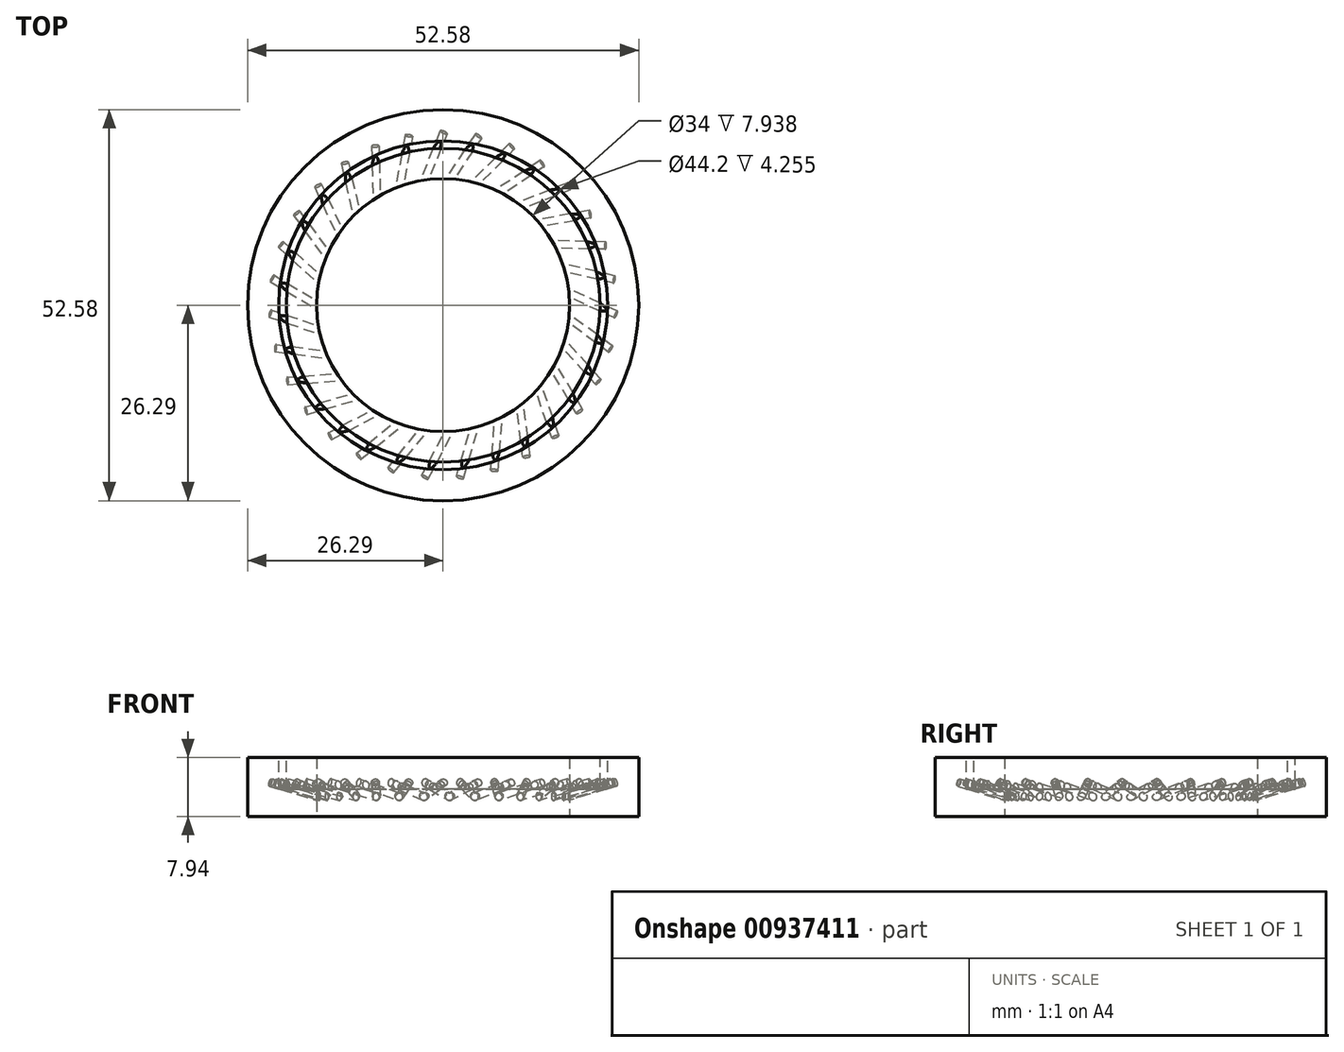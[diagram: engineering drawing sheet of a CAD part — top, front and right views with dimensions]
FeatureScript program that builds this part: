
annotation { "Feature Type Name" : "Feature", "Feature Type Description" : "" }
export const myFeature = defineFeature(function(context is Context, id is Id, definition is map)
    precondition{}
    {
        {
            var Q0;
            Q0=qCreatedBy(makeId("Top.planeOp"),FACE);
            var sketch = newSketch(context, id + "F0", { "sketchPlane" : qUnion([Q0])});
            skCircle(sketch, "E0", {"center": v(0, 0) * mm, "radius": 26.29 * mm});
            skSolve(sketch);
        }
        {
            var Q0;
            Q0=makeQuery(id+"F0.imprint","IMPRINT",FACE,{"disambiguationData":[TD([[makeQuery(id+"F0.imprint","IMPRINT",EDGE,{"derivedFrom":sQuery(id+"F0.wireOp",EDGE,"E0")}),1.0]])]});
            extrude(context, id + "F1", {"entities" : qUnion([Q0]), "depth" : 7.94 * mm, "offsetDistance" : 25.4 * mm});
        }
        {
            var Q0;
            Q0=qCreatedBy(makeId("Top.planeOp"),FACE);
            var sketch = newSketch(context, id + "F2", { "sketchPlane" : qUnion([Q0])});
            skCircle(sketch, "E1", {"center": v(0, 0) * mm, "radius": 17 * mm});
            skSolve(sketch);
        }
        {
            var Q0;
            Q0=qSketchRegion(id+"F2",true);
            extrude(context, id + "F3", {"entities" : qUnion([Q0]), "operationType" : NewBodyOperationType.REMOVE, "endBound" : BoundingType.THROUGH_ALL, "depth" : 7.94 * mm, "offsetDistance" : 25.4 * mm});
        }
        {
            var Q0;
            Q0=qCreatedBy(makeId("Right.planeOp"),FACE);
            var sketch = newSketch(context, id + "F4", { "sketchPlane" : qUnion([Q0])});
            skLineSegment(sketch, "E2", {"start": v(0, 0) * mm, "end": v(0, 143.33) * mm});
            skLineSegment(sketch, "E3", {"start": v(-8.9, 0) * mm, "end": v(-8.9, 70.97) * mm});
            skSolve(sketch);
        }
        {
            var Q0;
            Q0=qCreatedBy(makeId("Top.planeOp"),FACE);
            var sketch = newSketch(context, id + "F5", { "sketchPlane" : qUnion([Q0])});
            skLineSegment(sketch, "E4", {"start": v(0, 0) * mm, "end": v(29.86, 0) * mm});
            skSolve(sketch);
        }
        {
            var Q0;
            Q0=qCreatedBy(makeId("Right.planeOp"),FACE);
            var sketch = newSketch(context, id + "F6", { "sketchPlane" : qUnion([Q0])});
            skCircle(sketch, "E5", {"center": v(0, 54.1) * mm, "radius": 0.5 * mm});
            skSolve(sketch);
        }
        {
            var Q0;
            Q0=makeQuery(id+"F6.imprint","IMPRINT",FACE,{"disambiguationData":[TD([[makeQuery(id+"F6.imprint","IMPRINT",EDGE,{"derivedFrom":sQuery(id+"F6.wireOp",EDGE,"E5")}),1.0]])]});
            extrude(context, id + "F7", {"entities" : qUnion([Q0]), "depth" : 28.07 * mm, "offsetDistance" : 25.4 * mm});
        }
        {
            var Q0;
            Q0=makeQuery(id+"F7.opExtrude","SWEPT_BODY",BODY,{"disambiguationData":[OSD([sQuery(id+"F6.wireOp",EDGE,"E5")])]});
            var Q1;
            Q1=sQuery(id+"F4.wireOp",EDGE,"E2");
            transform(context, id + "F8", {"entities" : qUnion([Q0]), "transformType" : TransformType.ROTATION, "transformAxis" : qUnion([Q1]), "angle" : 20 * degree, "makeCopy" : false});
        }
        {
            var Q0;
            Q0=makeQuery(id+"F7.opExtrude","SWEPT_BODY",BODY,{"disambiguationData":[OSD([sQuery(id+"F6.wireOp",EDGE,"E5")])]});
            transform(context, id + "F9", {"entities" : qUnion([Q0]), "transformType" : TransformType.TRANSLATION_3D, "dx" : 0 * mm, "dy" : 0 * mm, "dz" : -58.42 * mm, "makeCopy" : false});
        }
        {
            var Q0;
            Q0=makeQuery(id+"F7.opExtrude","SWEPT_BODY",BODY,{"disambiguationData":[OSD([sQuery(id+"F6.wireOp",EDGE,"E5")])]});
            var Q1;
            Q1=sQuery(id+"F5.wireOp",EDGE,"E4");
            var Q2;
            Q2=sQuery(id+"F5.wireOp",EDGE,"E4");
            transform(context, id + "F10", {"entities" : qUnion([Q0]), "transformType" : TransformType.ROTATION, "transformAxis" : qUnion([Q2]), "angle" : 50 * degree, "makeCopy" : false});
        }
        {
            var Q0;
            Q0=makeQuery(id+"F7.opExtrude","SWEPT_BODY",BODY,{"disambiguationData":[OSD([sQuery(id+"F6.wireOp",EDGE,"E5")])]});
            var Q1;
            Q1=sQuery(id+"F4.wireOp",EDGE,"E2");
            var Q2;
            Q2=sQuery(id+"F4.wireOp",EDGE,"E3");
            transform(context, id + "F11", {"entities" : qUnion([Q0]), "transformType" : TransformType.ROTATION, "transformAxis" : qUnion([Q2]), "angle" : 55 * degree, "makeCopy" : false});
        }
        {
            var Q0;
            Q0=makeQuery(id+"F7.opExtrude","SWEPT_BODY",BODY,{"disambiguationData":[OSD([sQuery(id+"F6.wireOp",EDGE,"E5")])]});
            var Q1;
            Q1=sQuery(id+"F4.wireOp",EDGE,"E2");
            circularPattern(context, id + "F12", {"entities" : qUnion([Q0]), "axis" : qUnion([Q1]), "angle" : 360 * degree, "instanceCount" : 31, "equalSpace" : true});
        }
        {
            var Q0;
            Q0=makeQuery(id+"F7.opExtrude","SWEPT_BODY",BODY,{"disambiguationData":[OSD([sQuery(id+"F6.wireOp",EDGE,"E5")])]});
            var Q1;
            Q1=makeQuery(id+"F12.opPattern","COPY",BODY,{"derivedFrom":makeQuery(id+"F7.opExtrude","SWEPT_BODY",BODY,{"disambiguationData":[OSD([sQuery(id+"F6.wireOp",EDGE,"E5")])]}),"instanceName":"14"});
            var Q2;
            Q2=makeQuery(id+"F1.opExtrude","SWEPT_BODY",BODY,{"disambiguationData":[OSD([sQuery(id+"F0.wireOp",EDGE,"E0")])]});
            booleanBodies(context, id + "F13", {"operationType" : BooleanOperationType.SUBTRACTION, "tools" : qUnion([Q0, Q1]), "targets" : qUnion([Q2])});
        }
        {
            var Q0;
            Q0=makeQuery(id+"F12.opPattern","COPY",BODY,{"derivedFrom":makeQuery(id+"F7.opExtrude","SWEPT_BODY",BODY,{"disambiguationData":[OSD([sQuery(id+"F6.wireOp",EDGE,"E5")])]}),"instanceName":"30"});
            var Q1;
            Q1=makeQuery(id+"F12.opPattern","COPY",BODY,{"derivedFrom":makeQuery(id+"F7.opExtrude","SWEPT_BODY",BODY,{"disambiguationData":[OSD([sQuery(id+"F6.wireOp",EDGE,"E5")])]}),"instanceName":"28"});
            var Q2;
            Q2=makeQuery(id+"F12.opPattern","COPY",BODY,{"derivedFrom":makeQuery(id+"F7.opExtrude","SWEPT_BODY",BODY,{"disambiguationData":[OSD([sQuery(id+"F6.wireOp",EDGE,"E5")])]}),"instanceName":"26"});
            var Q3;
            Q3=makeQuery(id+"F12.opPattern","COPY",BODY,{"derivedFrom":makeQuery(id+"F7.opExtrude","SWEPT_BODY",BODY,{"disambiguationData":[OSD([sQuery(id+"F6.wireOp",EDGE,"E5")])]}),"instanceName":"24"});
            var Q4;
            Q4=makeQuery(id+"F12.opPattern","COPY",BODY,{"derivedFrom":makeQuery(id+"F7.opExtrude","SWEPT_BODY",BODY,{"disambiguationData":[OSD([sQuery(id+"F6.wireOp",EDGE,"E5")])]}),"instanceName":"22"});
            var Q5;
            Q5=makeQuery(id+"F1.opExtrude","SWEPT_BODY",BODY,{"disambiguationData":[OSD([sQuery(id+"F0.wireOp",EDGE,"E0")])]});
            booleanBodies(context, id + "F14", {"operationType" : BooleanOperationType.SUBTRACTION, "tools" : qUnion([Q0, Q1, Q2, Q3, Q4]), "targets" : qUnion([Q5])});
        }
        {
            var Q0;
            Q0=makeQuery(id+"F12.opPattern","COPY",BODY,{"derivedFrom":makeQuery(id+"F7.opExtrude","SWEPT_BODY",BODY,{"disambiguationData":[OSD([sQuery(id+"F6.wireOp",EDGE,"E5")])]}),"instanceName":"20"});
            var Q1;
            Q1=makeQuery(id+"F12.opPattern","COPY",BODY,{"derivedFrom":makeQuery(id+"F7.opExtrude","SWEPT_BODY",BODY,{"disambiguationData":[OSD([sQuery(id+"F6.wireOp",EDGE,"E5")])]}),"instanceName":"18"});
            var Q2;
            Q2=makeQuery(id+"F12.opPattern","COPY",BODY,{"derivedFrom":makeQuery(id+"F7.opExtrude","SWEPT_BODY",BODY,{"disambiguationData":[OSD([sQuery(id+"F6.wireOp",EDGE,"E5")])]}),"instanceName":"16"});
            var Q3;
            Q3=makeQuery(id+"F12.opPattern","COPY",BODY,{"derivedFrom":makeQuery(id+"F7.opExtrude","SWEPT_BODY",BODY,{"disambiguationData":[OSD([sQuery(id+"F6.wireOp",EDGE,"E5")])]}),"instanceName":"13"});
            var Q4;
            Q4=makeQuery(id+"F12.opPattern","COPY",BODY,{"derivedFrom":makeQuery(id+"F7.opExtrude","SWEPT_BODY",BODY,{"disambiguationData":[OSD([sQuery(id+"F6.wireOp",EDGE,"E5")])]}),"instanceName":"11"});
            var Q5;
            Q5=makeQuery(id+"F12.opPattern","COPY",BODY,{"derivedFrom":makeQuery(id+"F7.opExtrude","SWEPT_BODY",BODY,{"disambiguationData":[OSD([sQuery(id+"F6.wireOp",EDGE,"E5")])]}),"instanceName":"9"});
            var Q6;
            Q6=makeQuery(id+"F12.opPattern","COPY",BODY,{"derivedFrom":makeQuery(id+"F7.opExtrude","SWEPT_BODY",BODY,{"disambiguationData":[OSD([sQuery(id+"F6.wireOp",EDGE,"E5")])]}),"instanceName":"7"});
            var Q7;
            Q7=makeQuery(id+"F12.opPattern","COPY",BODY,{"derivedFrom":makeQuery(id+"F7.opExtrude","SWEPT_BODY",BODY,{"disambiguationData":[OSD([sQuery(id+"F6.wireOp",EDGE,"E5")])]}),"instanceName":"5"});
            var Q8;
            Q8=makeQuery(id+"F12.opPattern","COPY",BODY,{"derivedFrom":makeQuery(id+"F7.opExtrude","SWEPT_BODY",BODY,{"disambiguationData":[OSD([sQuery(id+"F6.wireOp",EDGE,"E5")])]}),"instanceName":"3"});
            var Q9;
            Q9=makeQuery(id+"F12.opPattern","COPY",BODY,{"derivedFrom":makeQuery(id+"F7.opExtrude","SWEPT_BODY",BODY,{"disambiguationData":[OSD([sQuery(id+"F6.wireOp",EDGE,"E5")])]}),"instanceName":"1"});
            var Q10;
            Q10=makeQuery(id+"F1.opExtrude","SWEPT_BODY",BODY,{"disambiguationData":[OSD([sQuery(id+"F0.wireOp",EDGE,"E0")])]});
            booleanBodies(context, id + "F15", {"operationType" : BooleanOperationType.SUBTRACTION, "tools" : qUnion([Q0, Q1, Q2, Q3, Q4, Q5, Q6, Q7, Q8, Q9]), "targets" : qUnion([Q10])});
        }
        {
            var Q0;
            Q0=makeQuery(id+"F12.opPattern","COPY",BODY,{"derivedFrom":makeQuery(id+"F7.opExtrude","SWEPT_BODY",BODY,{"disambiguationData":[OSD([sQuery(id+"F6.wireOp",EDGE,"E5")])]}),"instanceName":"29"});
            var Q1;
            Q1=makeQuery(id+"F12.opPattern","COPY",BODY,{"derivedFrom":makeQuery(id+"F7.opExtrude","SWEPT_BODY",BODY,{"disambiguationData":[OSD([sQuery(id+"F6.wireOp",EDGE,"E5")])]}),"instanceName":"27"});
            var Q2;
            Q2=makeQuery(id+"F12.opPattern","COPY",BODY,{"derivedFrom":makeQuery(id+"F7.opExtrude","SWEPT_BODY",BODY,{"disambiguationData":[OSD([sQuery(id+"F6.wireOp",EDGE,"E5")])]}),"instanceName":"25"});
            var Q3;
            Q3=makeQuery(id+"F12.opPattern","COPY",BODY,{"derivedFrom":makeQuery(id+"F7.opExtrude","SWEPT_BODY",BODY,{"disambiguationData":[OSD([sQuery(id+"F6.wireOp",EDGE,"E5")])]}),"instanceName":"23"});
            var Q4;
            Q4=makeQuery(id+"F12.opPattern","COPY",BODY,{"derivedFrom":makeQuery(id+"F7.opExtrude","SWEPT_BODY",BODY,{"disambiguationData":[OSD([sQuery(id+"F6.wireOp",EDGE,"E5")])]}),"instanceName":"21"});
            var Q5;
            Q5=makeQuery(id+"F12.opPattern","COPY",BODY,{"derivedFrom":makeQuery(id+"F7.opExtrude","SWEPT_BODY",BODY,{"disambiguationData":[OSD([sQuery(id+"F6.wireOp",EDGE,"E5")])]}),"instanceName":"19"});
            var Q6;
            Q6=makeQuery(id+"F12.opPattern","COPY",BODY,{"derivedFrom":makeQuery(id+"F7.opExtrude","SWEPT_BODY",BODY,{"disambiguationData":[OSD([sQuery(id+"F6.wireOp",EDGE,"E5")])]}),"instanceName":"17"});
            var Q7;
            Q7=makeQuery(id+"F12.opPattern","COPY",BODY,{"derivedFrom":makeQuery(id+"F7.opExtrude","SWEPT_BODY",BODY,{"disambiguationData":[OSD([sQuery(id+"F6.wireOp",EDGE,"E5")])]}),"instanceName":"15"});
            var Q8;
            Q8=makeQuery(id+"F12.opPattern","COPY",BODY,{"derivedFrom":makeQuery(id+"F7.opExtrude","SWEPT_BODY",BODY,{"disambiguationData":[OSD([sQuery(id+"F6.wireOp",EDGE,"E5")])]}),"instanceName":"12"});
            var Q9;
            Q9=makeQuery(id+"F12.opPattern","COPY",BODY,{"derivedFrom":makeQuery(id+"F7.opExtrude","SWEPT_BODY",BODY,{"disambiguationData":[OSD([sQuery(id+"F6.wireOp",EDGE,"E5")])]}),"instanceName":"10"});
            var Q10;
            Q10=makeQuery(id+"F12.opPattern","COPY",BODY,{"derivedFrom":makeQuery(id+"F7.opExtrude","SWEPT_BODY",BODY,{"disambiguationData":[OSD([sQuery(id+"F6.wireOp",EDGE,"E5")])]}),"instanceName":"8"});
            var Q11;
            Q11=makeQuery(id+"F12.opPattern","COPY",BODY,{"derivedFrom":makeQuery(id+"F7.opExtrude","SWEPT_BODY",BODY,{"disambiguationData":[OSD([sQuery(id+"F6.wireOp",EDGE,"E5")])]}),"instanceName":"6"});
            var Q12;
            Q12=makeQuery(id+"F12.opPattern","COPY",BODY,{"derivedFrom":makeQuery(id+"F7.opExtrude","SWEPT_BODY",BODY,{"disambiguationData":[OSD([sQuery(id+"F6.wireOp",EDGE,"E5")])]}),"instanceName":"4"});
            var Q13;
            Q13=makeQuery(id+"F12.opPattern","COPY",BODY,{"derivedFrom":makeQuery(id+"F7.opExtrude","SWEPT_BODY",BODY,{"disambiguationData":[OSD([sQuery(id+"F6.wireOp",EDGE,"E5")])]}),"instanceName":"2"});
            var Q14;
            Q14=makeQuery(id+"F1.opExtrude","SWEPT_BODY",BODY,{"disambiguationData":[OSD([sQuery(id+"F0.wireOp",EDGE,"E0")])]});
            booleanBodies(context, id + "F16", {"operationType" : BooleanOperationType.SUBTRACTION, "tools" : qUnion([Q0, Q1, Q2, Q3, Q4, Q5, Q6, Q7, Q8, Q9, Q10, Q11, Q12, Q13]), "targets" : qUnion([Q14])});
        }
        {
            var Q0;
            Q0=makeQuery(id+"F1.opExtrude","CAP_FACE",FACE,{"disambiguationData":[OSD([sQuery(id+"F0.wireOp",EDGE,"E0")])],"isStart":false});
            var sketch = newSketch(context, id + "F17", { "sketchPlane" : qUnion([Q0])});
            skCircle(sketch, "E6", {"center": v(0, 0) * mm, "radius": 22.1 * mm});
            skCircle(sketch, "E7", {"center": v(0, 0) * mm, "radius": 21.08 * mm});
            skSolve(sketch);
        }
        {
            var Q0;
            Q0=makeQuery(id+"F17.imprint","IMPRINT",FACE,{"disambiguationData":[TD([[makeQuery(id+"F17.imprint","IMPRINT",EDGE,{"derivedFrom":sQuery(id+"F17.wireOp",EDGE,"E6")}),1.0]])]});
            var Q1;
            Q1=sQuery(id+"F17.wireOp",EDGE,"E6");
            var Q2;
            Q2=sQuery(id+"F17.wireOp",EDGE,"E7");
            extrude(context, id + "F18", {"entities" : qUnion([Q0]), "operationType" : NewBodyOperationType.REMOVE, "surfaceEntities" : qUnion([Q1, Q2]), "oppositeDirection" : true, "depth" : 4.25 * mm, "offsetDistance" : 25.4 * mm});
        }
    });
